# Revit family: BC_Hitachi_Samurai-Water-Cooled_LOD400
name_source: partatom
category: Equipement de génie climatique
revit_build: Autodesk Revit 2017 (Build: 20160225_1515(x64)
units: mm (PartAtom-declared; Revit-internal decimal feet)

## family parameters
Basée sur le plan de construction = Non
Cote de connecteur circulaire = Utiliser le diamètre
Couper avec des vides une fois chargée = Non
Numéro OmniClass = 23.75.10.24
Partagée = Non
Point de calcul de pièce = Non
Titre OmniClass = Cooling and Freeze Plant
Toujours verticalement = Oui
Type d'élément = Normal

## types (3) — shared parameters
Color = Natural Grey
Description = Samurai - Water Cooled
Fabricant = HITACHI
Frequency (Hz) = 50
Inlet Gas Diameter = 54 mm
Maximum AC Voltage = 440 V
Minimum AC Voltage = 360 V
Modèle = Samurai - Water Cooled
Nominal Voltage = 400 V
Operating mode = Cooling [1]
Outlet Gas Diameter = 29 mm
Overall Height = 1681 mm
Overall Length = 1271 mm
Overall Width = 806 mm
Refrigerant Quantity = 1.00 kg
Refrigerant Type = R134a

## per-type parameters (varying)
- RCME 40CLH1: Cooling Capacity=135 kW; Cooling Maximum Flow - Evaporator Water Side=188.3 m³/h; Cooling Minimum Flow - Evaporator Water Side=54.4 m³/h; Cooling Nominal Current=54 A; Cooling Nominal Flow - Evaporator Water Side=86.8 m³/h; Cooling Nominal Input Power=32 kW; Cooling Pressure Drop at nominal flow - Evaporator Water Side=20.0 kPa; Cooling Sound Level Low (dB)=82; Cooling Sound Level Silent (dB)=88; Cooling power=32 kW; Energy efficiency ratio (EER)=4.22; Heating Maximum Flow - Evaporator Water Side=78.5 m³/h; Heating Minimum Flow - Evaporator Water Side=120.2 m³/h; Inlet Water Diameter=368 mm; Low Noise Model at 10m (dB(A))=54; Maximum Current for cable sizing=73 A; Maximum Input Power for cable sizing=33 kW; Maximum Starting Current for cable sizing=179 A; Packing Weight=750.00 kg; Standard Noise Level Model at 10m (dB(A))=60; Starting Current=179 A; Super Low Noise Model (dB(A))=72; Super Low Noise Model at 10m (dB(A))=44; Water Outlet Diameter=368 mm; Weight in operation=765.00 kg
- RCME 50CLH1: Cooling Capacity=175 kW; Cooling Maximum Flow - Evaporator Water Side=242.3 m³/h; Cooling Minimum Flow - Evaporator Water Side=69.8 m³/h; Cooling Nominal Current=69 A; Cooling Nominal Flow - Evaporator Water Side=111.6 m³/h; Cooling Nominal Input Power=42 kW; Cooling Pressure Drop at nominal flow - Evaporator Water Side=21.5 kPa; Cooling Sound Level Low (dB)=83; Cooling Sound Level Silent (dB)=89; Cooling power=42 kW; Energy efficiency ratio (EER)=4.19; Heating Maximum Flow - Evaporator Water Side=100.8 m³/h; Heating Minimum Flow - Evaporator Water Side=155.9 m³/h; Inlet Water Diameter=673 mm; Low Noise Model at 10m (dB(A))=55; Maximum Current for cable sizing=93 A; Maximum Input Power for cable sizing=43 kW; Maximum Starting Current for cable sizing=240 A; Packing Weight=810.00 kg; Standard Noise Level Model at 10m (dB(A))=61; Starting Current=240 A; Super Low Noise Model (dB(A))=73; Super Low Noise Model at 10m (dB(A))=45; Water Outlet Diameter=673 mm; Weight in operation=835.00 kg
- RCME 60CLH1: Cooling Capacity=215 kW; Cooling Maximum Flow - Evaporator Water Side=296.3 m³/h; Cooling Minimum Flow - Evaporator Water Side=85.3 m³/h; Cooling Nominal Current=87 A; Cooling Nominal Flow - Evaporator Water Side=136.1 m³/h; Cooling Nominal Input Power=52 kW; Cooling Pressure Drop at nominal flow - Evaporator Water Side=19.7 kPa; Cooling Sound Level Low (dB)=84; Cooling Sound Level Silent (dB)=90; Cooling power=52 kW; Energy efficiency ratio (EER)=4.1; Heating Maximum Flow - Evaporator Water Side=123.1 m³/h; Heating Minimum Flow - Evaporator Water Side=194.8 m³/h; Inlet Water Diameter=978 mm; Low Noise Model at 10m (dB(A))=56; Maximum Current for cable sizing=116 A; Maximum Input Power for cable sizing=54 kW; Maximum Starting Current for cable sizing=240 A; Packing Weight=875.00 kg; Standard Noise Level Model at 10m (dB(A))=62; Starting Current=240 A; Super Low Noise Model (dB(A))=74; Super Low Noise Model at 10m (dB(A))=46; Water Outlet Diameter=978 mm; Weight in operation=900.00 kg

note: column(s) folded — value = type name in every type: Commentaires du type
